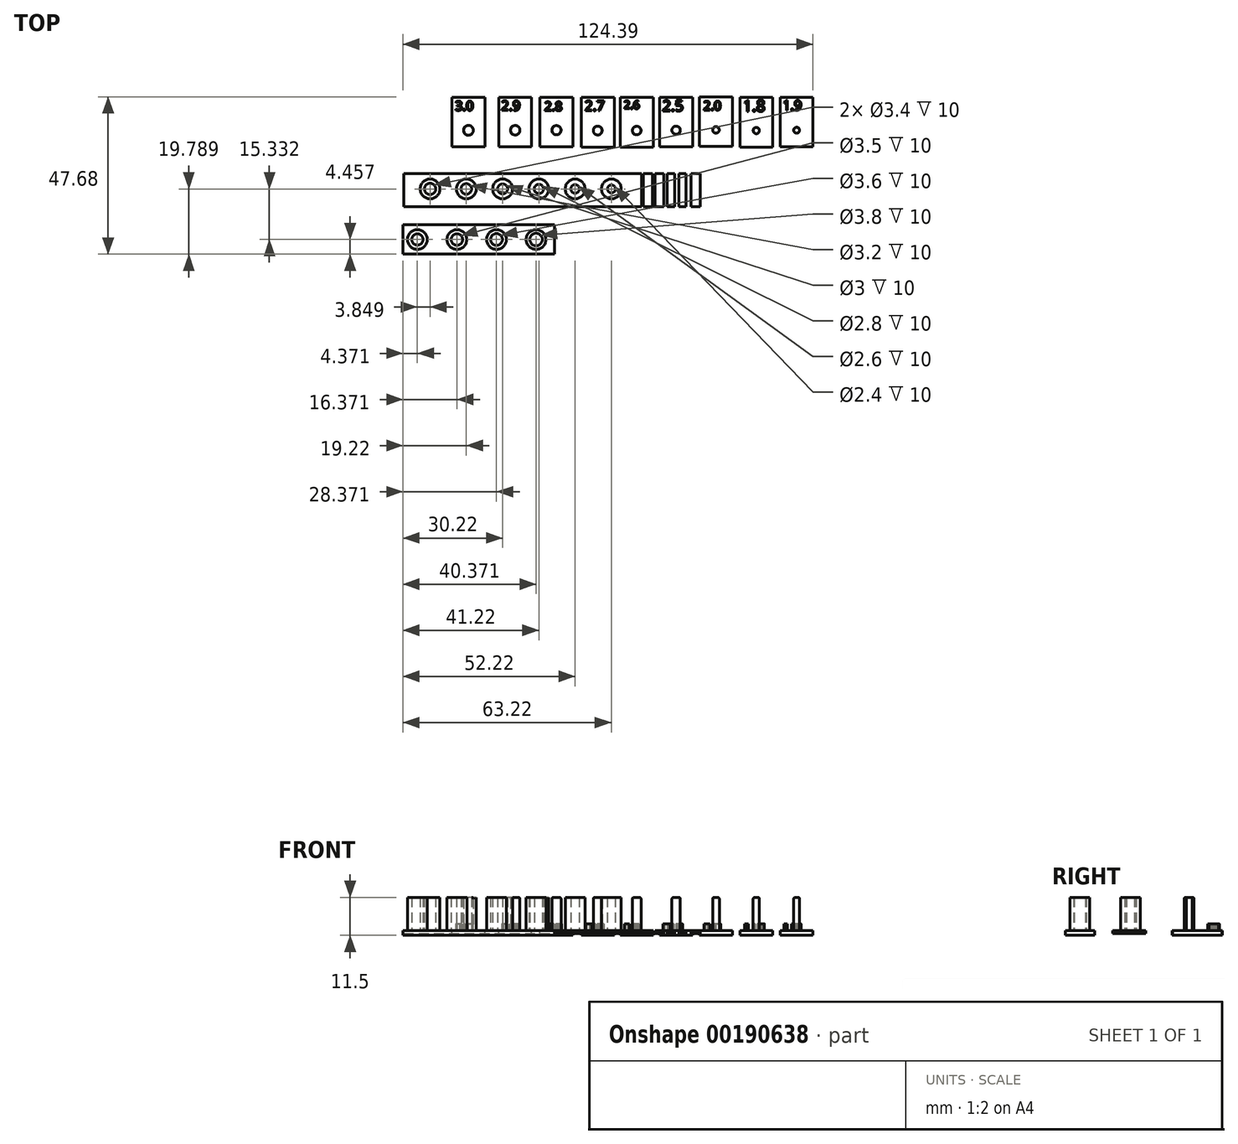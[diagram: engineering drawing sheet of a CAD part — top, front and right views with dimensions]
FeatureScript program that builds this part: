
annotation { "Feature Type Name" : "Feature", "Feature Type Description" : "" }
export const myFeature = defineFeature(function(context is Context, id is Id, definition is map)
    precondition{}
    {
        {
            var Q0;
            Q0=qCreatedBy(makeId("Top.planeOp"),FACE);
            var sketch = newSketch(context, id + "F0", { "sketchPlane" : qUnion([Q0])});
            skLineSegment(sketch, "E0.bottom", {"start": v(-35, 10) * mm, "end": v(55, 10) * mm});
            skLineSegment(sketch, "E0.top", {"start": v(-35, 0) * mm, "end": v(55, 0) * mm});
            skLineSegment(sketch, "E0.left", {"start": v(-35, 10) * mm, "end": v(-35, 0) * mm});
            skLineSegment(sketch, "E0.right", {"start": v(55, 10) * mm, "end": v(55, 0) * mm});
            skCircle(sketch, "E1", {"center": v(-27, 5.35) * mm, "radius": 3 * mm});
            skCircle(sketch, "E2", {"center": v(-16, 5.35) * mm, "radius": 3 * mm});
            skCircle(sketch, "E3", {"center": v(-5, 5.35) * mm, "radius": 3 * mm});
            skCircle(sketch, "E4", {"center": v(6, 5.35) * mm, "radius": 3 * mm});
            skCircle(sketch, "E5", {"center": v(17, 5.35) * mm, "radius": 3 * mm});
            skCircle(sketch, "E6", {"center": v(28, 5.35) * mm, "radius": 3 * mm});
            skCircle(sketch, "E7", {"center": v(28, 5.35) * mm, "radius": 1.2 * mm});
            skCircle(sketch, "E8", {"center": v(17, 5.35) * mm, "radius": 1.3 * mm});
            skCircle(sketch, "E9", {"center": v(6, 5.35) * mm, "radius": 1.4 * mm});
            skCircle(sketch, "E10", {"center": v(-5, 5.35) * mm, "radius": 1.5 * mm});
            skCircle(sketch, "E11", {"center": v(-16, 5.35) * mm, "radius": 1.6 * mm});
            skCircle(sketch, "E12", {"center": v(-27, 5.35) * mm, "radius": 1.7 * mm});
            skLineSegment(sketch, "E13.bottom", {"start": v(52.19, 10) * mm, "end": v(50.69, 10) * mm});
            skLineSegment(sketch, "E13.top", {"start": v(52.19, 0) * mm, "end": v(50.69, 0) * mm});
            skLineSegment(sketch, "E13.left", {"start": v(52.19, 10) * mm, "end": v(52.19, 0) * mm});
            skLineSegment(sketch, "E13.right", {"start": v(50.69, 10) * mm, "end": v(50.69, 0) * mm});
            skLineSegment(sketch, "E14.bottom", {"start": v(48.47, 10) * mm, "end": v(47.22, 10) * mm});
            skLineSegment(sketch, "E14.top", {"start": v(48.47, 0) * mm, "end": v(47.22, 0) * mm});
            skLineSegment(sketch, "E14.left", {"start": v(48.47, 10) * mm, "end": v(48.47, 0) * mm});
            skLineSegment(sketch, "E14.right", {"start": v(47.22, 10) * mm, "end": v(47.22, 0) * mm});
            skLineSegment(sketch, "E15.bottom", {"start": v(44.89, 10) * mm, "end": v(43.89, 10) * mm});
            skLineSegment(sketch, "E15.top", {"start": v(44.89, 0) * mm, "end": v(43.89, 0) * mm});
            skLineSegment(sketch, "E15.left", {"start": v(44.89, 10) * mm, "end": v(44.89, 0) * mm});
            skLineSegment(sketch, "E15.right", {"start": v(43.89, 10) * mm, "end": v(43.89, 0) * mm});
            skLineSegment(sketch, "E16.bottom", {"start": v(41.17, 10) * mm, "end": v(40.42, 10) * mm});
            skLineSegment(sketch, "E16.top", {"start": v(41.17, 0) * mm, "end": v(40.42, 0) * mm});
            skLineSegment(sketch, "E16.left", {"start": v(41.17, 10) * mm, "end": v(41.17, 0) * mm});
            skLineSegment(sketch, "E16.right", {"start": v(40.42, 10) * mm, "end": v(40.42, 0) * mm});
            skLineSegment(sketch, "E17.bottom", {"start": v(37.71, 10) * mm, "end": v(37.21, 10) * mm});
            skLineSegment(sketch, "E17.top", {"start": v(37.71, 0) * mm, "end": v(37.21, 0) * mm});
            skLineSegment(sketch, "E17.left", {"start": v(37.71, 10) * mm, "end": v(37.71, 0) * mm});
            skLineSegment(sketch, "E17.right", {"start": v(37.21, 10) * mm, "end": v(37.21, 0) * mm});
            skSolve(sketch);
        }
        {
            var Q0;
            Q0=makeQuery(id+"F0.imprint","IMPRINT",FACE,{"disambiguationData":[TD([[makeQuery(id+"F0.imprint","IMPRINT",EDGE,{"derivedFrom":sQuery(id+"F0.wireOp",EDGE,"E6")}),1.0]])]});
            var Q1;
            {var subQ0=sQuery(id+"F0.wireOp",EDGE,"E0.right");Q1=makeQuery(id+"F0.imprint","IMPRINT",FACE,{"disambiguationData":[TD([[makeQuery(id+"F0.imprint","IMPRINT",EDGE,{"derivedFrom":subQ0}),-1.0]])]});}
            var Q2;
            {var subQ0=sQuery(id+"F0.wireOp",EDGE,"E16.right");Q2=makeQuery(id+"F0.imprint","IMPRINT",FACE,{"disambiguationData":[TD([[makeQuery(id+"F0.imprint","IMPRINT",EDGE,{"derivedFrom":subQ0}),-1.0]])]});}
            var Q3;
            {var subQ0=sQuery(id+"F0.wireOp",EDGE,"E15.right");Q3=makeQuery(id+"F0.imprint","IMPRINT",FACE,{"disambiguationData":[TD([[makeQuery(id+"F0.imprint","IMPRINT",EDGE,{"derivedFrom":subQ0}),-1.0]])]});}
            var Q4;
            {var subQ0=sQuery(id+"F0.wireOp",EDGE,"E14.right");Q4=makeQuery(id+"F0.imprint","IMPRINT",FACE,{"disambiguationData":[TD([[makeQuery(id+"F0.imprint","IMPRINT",EDGE,{"derivedFrom":subQ0}),-1.0]])]});}
            var Q5;
            {var subQ0=sQuery(id+"F0.wireOp",EDGE,"E13.right");Q5=makeQuery(id+"F0.imprint","IMPRINT",FACE,{"disambiguationData":[TD([[makeQuery(id+"F0.imprint","IMPRINT",EDGE,{"derivedFrom":subQ0}),-1.0]])]});}
            var Q6;
            Q6=makeQuery(id+"F0.imprint","IMPRINT",FACE,{"disambiguationData":[TD([[makeQuery(id+"F0.imprint","IMPRINT",EDGE,{"derivedFrom":sQuery(id+"F0.wireOp",EDGE,"E4")}),1.0]])]});
            var Q7;
            Q7=makeQuery(id+"F0.imprint","IMPRINT",FACE,{"disambiguationData":[TD([[makeQuery(id+"F0.imprint","IMPRINT",EDGE,{"derivedFrom":sQuery(id+"F0.wireOp",EDGE,"E5")}),1.0]])]});
            var Q8;
            Q8=makeQuery(id+"F0.imprint","IMPRINT",FACE,{"disambiguationData":[TD([[makeQuery(id+"F0.imprint","IMPRINT",EDGE,{"derivedFrom":sQuery(id+"F0.wireOp",EDGE,"E9")}),1.0]])]});
            var Q9;
            Q9=makeQuery(id+"F0.imprint","IMPRINT",FACE,{"disambiguationData":[TD([[makeQuery(id+"F0.imprint","IMPRINT",EDGE,{"derivedFrom":sQuery(id+"F0.wireOp",EDGE,"E10")}),1.0]])]});
            var Q10;
            Q10=makeQuery(id+"F0.imprint","IMPRINT",FACE,{"disambiguationData":[TD([[makeQuery(id+"F0.imprint","IMPRINT",EDGE,{"derivedFrom":sQuery(id+"F0.wireOp",EDGE,"E7")}),1.0]])]});
            var Q11;
            Q11=makeQuery(id+"F0.imprint","IMPRINT",FACE,{"disambiguationData":[TD([[makeQuery(id+"F0.imprint","IMPRINT",EDGE,{"derivedFrom":sQuery(id+"F0.wireOp",EDGE,"E8")}),1.0]])]});
            var Q12;
            Q12=makeQuery(id+"F0.imprint","IMPRINT",FACE,{"disambiguationData":[TD([[makeQuery(id+"F0.imprint","IMPRINT",EDGE,{"derivedFrom":sQuery(id+"F0.wireOp",EDGE,"E11")}),1.0]])]});
            var Q13;
            Q13=makeQuery(id+"F0.imprint","IMPRINT",FACE,{"disambiguationData":[TD([[makeQuery(id+"F0.imprint","IMPRINT",EDGE,{"derivedFrom":sQuery(id+"F0.wireOp",EDGE,"E12")}),1.0]])]});
            var Q14;
            Q14=makeQuery(id+"F0.imprint","IMPRINT",FACE,{"disambiguationData":[TD([[makeQuery(id+"F0.imprint","IMPRINT",EDGE,{"derivedFrom":sQuery(id+"F0.wireOp",EDGE,"E1")}),1.0]])]});
            var Q15;
            Q15=makeQuery(id+"F0.imprint","IMPRINT",FACE,{"disambiguationData":[TD([[makeQuery(id+"F0.imprint","IMPRINT",EDGE,{"derivedFrom":sQuery(id+"F0.wireOp",EDGE,"E2")}),1.0]])]});
            var Q16;
            Q16=makeQuery(id+"F0.imprint","IMPRINT",FACE,{"disambiguationData":[TD([[makeQuery(id+"F0.imprint","IMPRINT",EDGE,{"derivedFrom":sQuery(id+"F0.wireOp",EDGE,"E3")}),1.0]])]});
            var Q17;
            {var subQ1=sQuery(id+"F0.wireOp",EDGE,"E0.left");Q17=makeQuery(id+"F0.imprint","IMPRINT",FACE,{"disambiguationData":[TD([[makeQuery(id+"F0.imprint","IMPRINT",EDGE,{"derivedFrom":subQ1}),1.0]])]});}
            var Q18;
            Q18=makeQuery(id+"F0.imprint","IMPRINT",FACE,{"disambiguationData":[TD([[makeQuery(id+"F0.imprint","IMPRINT",EDGE,{"derivedFrom":sQuery(id+"F0.wireOp",EDGE,"E15.bottom")}),1.0]])]});
            var Q19;
            Q19=makeQuery(id+"F0.imprint","IMPRINT",FACE,{"disambiguationData":[TD([[makeQuery(id+"F0.imprint","IMPRINT",EDGE,{"derivedFrom":sQuery(id+"F0.wireOp",EDGE,"E16.bottom")}),1.0]])]});
            var Q20;
            Q20=makeQuery(id+"F0.imprint","IMPRINT",FACE,{"disambiguationData":[TD([[makeQuery(id+"F0.imprint","IMPRINT",EDGE,{"derivedFrom":sQuery(id+"F0.wireOp",EDGE,"E13.bottom")}),1.0]])]});
            var Q21;
            Q21=makeQuery(id+"F0.imprint","IMPRINT",FACE,{"disambiguationData":[TD([[makeQuery(id+"F0.imprint","IMPRINT",EDGE,{"derivedFrom":sQuery(id+"F0.wireOp",EDGE,"E14.bottom")}),1.0]])]});
            var Q22;
            Q22=makeQuery(id+"F0.imprint","IMPRINT",FACE,{"disambiguationData":[TD([[makeQuery(id+"F0.imprint","IMPRINT",EDGE,{"derivedFrom":sQuery(id+"F0.wireOp",EDGE,"E17.bottom")}),1.0]])]});
            extrude(context, id + "F1", {"entities" : qUnion([Q0, Q1, Q2, Q3, Q4, Q5, Q6, Q7, Q8, Q9, Q10, Q11, Q12, Q13, Q14, Q15, Q16, Q17, Q18, Q19, Q20, Q21, Q22]), "oppositeDirection" : true, "depth" : 1 * mm});
        }
        {
            var Q0;
            Q0=makeQuery(id+"F0.imprint","IMPRINT",FACE,{"disambiguationData":[TD([[makeQuery(id+"F0.imprint","IMPRINT",EDGE,{"derivedFrom":sQuery(id+"F0.wireOp",EDGE,"E1")}),1.0]])]});
            var Q1;
            Q1=makeQuery(id+"F0.imprint","IMPRINT",FACE,{"disambiguationData":[TD([[makeQuery(id+"F0.imprint","IMPRINT",EDGE,{"derivedFrom":sQuery(id+"F0.wireOp",EDGE,"E2")}),1.0]])]});
            var Q2;
            Q2=makeQuery(id+"F0.imprint","IMPRINT",FACE,{"disambiguationData":[TD([[makeQuery(id+"F0.imprint","IMPRINT",EDGE,{"derivedFrom":sQuery(id+"F0.wireOp",EDGE,"E3")}),1.0]])]});
            var Q3;
            Q3=makeQuery(id+"F0.imprint","IMPRINT",FACE,{"disambiguationData":[TD([[makeQuery(id+"F0.imprint","IMPRINT",EDGE,{"derivedFrom":sQuery(id+"F0.wireOp",EDGE,"E4")}),1.0]])]});
            var Q4;
            Q4=makeQuery(id+"F0.imprint","IMPRINT",FACE,{"disambiguationData":[TD([[makeQuery(id+"F0.imprint","IMPRINT",EDGE,{"derivedFrom":sQuery(id+"F0.wireOp",EDGE,"E5")}),1.0]])]});
            var Q5;
            Q5=makeQuery(id+"F0.imprint","IMPRINT",FACE,{"disambiguationData":[TD([[makeQuery(id+"F0.imprint","IMPRINT",EDGE,{"derivedFrom":sQuery(id+"F0.wireOp",EDGE,"E6")}),1.0]])]});
            var Q6;
            Q6=makeQuery(id+"F0.imprint","IMPRINT",FACE,{"disambiguationData":[TD([[makeQuery(id+"F0.imprint","IMPRINT",EDGE,{"derivedFrom":sQuery(id+"F0.wireOp",EDGE,"PQmnJwLJ-Gn6O-ht3s-PqNv-8H9YZ1rAoUPC.bottom")}),-1.0]])]});
            var Q7;
            Q7=makeQuery(id+"F0.imprint","IMPRINT",FACE,{"disambiguationData":[TD([[makeQuery(id+"F0.imprint","IMPRINT",EDGE,{"derivedFrom":sQuery(id+"F0.wireOp",EDGE,"UL6PvTcp-d3gB-frWF-roNd-aRTeFT7Vgu0b.bottom")}),-1.0]])]});
            var Q8;
            Q8=makeQuery(id+"F0.imprint","IMPRINT",FACE,{"disambiguationData":[TD([[makeQuery(id+"F0.imprint","IMPRINT",EDGE,{"derivedFrom":sQuery(id+"F0.wireOp",EDGE,"dWqF2f6u-Qhn5-39Qu-3Qdw-AeupGA2DbPDi.bottom")}),-1.0]])]});
            var Q9;
            Q9=makeQuery(id+"F0.imprint","IMPRINT",FACE,{"disambiguationData":[TD([[makeQuery(id+"F0.imprint","IMPRINT",EDGE,{"derivedFrom":sQuery(id+"F0.wireOp",EDGE,"3pZbBdGt-NIDK-vHJ1-jkmm-BDyZuHJENsoI.bottom")}),-1.0]])]});
            var Q10;
            Q10=makeQuery(id+"F0.imprint","IMPRINT",FACE,{"disambiguationData":[TD([[makeQuery(id+"F0.imprint","IMPRINT",EDGE,{"derivedFrom":sQuery(id+"F0.wireOp",EDGE,"8ss7ZRCM-gOKD-5URm-W4XT-u9E1LTYDyoXy.bottom")}),-1.0]])]});
            var Q11;
            Q11=makeQuery(id+"F0.imprint","IMPRINT",FACE,{"disambiguationData":[TD([[makeQuery(id+"F0.imprint","IMPRINT",EDGE,{"derivedFrom":sQuery(id+"F0.wireOp",EDGE,"E17.bottom")}),1.0]])]});
            var Q12;
            Q12=makeQuery(id+"F0.imprint","IMPRINT",FACE,{"disambiguationData":[TD([[makeQuery(id+"F0.imprint","IMPRINT",EDGE,{"derivedFrom":sQuery(id+"F0.wireOp",EDGE,"E16.bottom")}),1.0]])]});
            var Q13;
            Q13=makeQuery(id+"F0.imprint","IMPRINT",FACE,{"disambiguationData":[TD([[makeQuery(id+"F0.imprint","IMPRINT",EDGE,{"derivedFrom":sQuery(id+"F0.wireOp",EDGE,"E15.bottom")}),1.0]])]});
            var Q14;
            Q14=makeQuery(id+"F0.imprint","IMPRINT",FACE,{"disambiguationData":[TD([[makeQuery(id+"F0.imprint","IMPRINT",EDGE,{"derivedFrom":sQuery(id+"F0.wireOp",EDGE,"E14.bottom")}),1.0]])]});
            var Q15;
            Q15=makeQuery(id+"F0.imprint","IMPRINT",FACE,{"disambiguationData":[TD([[makeQuery(id+"F0.imprint","IMPRINT",EDGE,{"derivedFrom":sQuery(id+"F0.wireOp",EDGE,"E13.bottom")}),1.0]])]});
            extrude(context, id + "F2", {"entities" : qUnion([Q0, Q1, Q2, Q3, Q4, Q5, Q6, Q7, Q8, Q9, Q10, Q11, Q12, Q13, Q14, Q15]), "operationType" : NewBodyOperationType.ADD, "depth" : 10 * mm});
        }
        {
            var Q0;
            Q0=qCreatedBy(makeId("Top.planeOp"),FACE);
            var sketch = newSketch(context, id + "F3", { "sketchPlane" : qUnion([Q0])});
            skLineSegment(sketch, "E18.bottom", {"start": v(-35.22, -5.53) * mm, "end": v(10.7, -5.53) * mm});
            skLineSegment(sketch, "E18.top", {"start": v(-35.22, -14.44) * mm, "end": v(10.7, -14.44) * mm});
            skLineSegment(sketch, "E18.left", {"start": v(-35.22, -5.53) * mm, "end": v(-35.22, -14.44) * mm});
            skLineSegment(sketch, "E18.right", {"start": v(10.7, -5.53) * mm, "end": v(10.7, -14.44) * mm});
            skCircle(sketch, "E19", {"center": v(-30.85, -9.98) * mm, "radius": 3 * mm});
            skCircle(sketch, "E20.1.0.0", {"center": v(-18.85, -9.98) * mm, "radius": 3 * mm});
            skCircle(sketch, "E20.2.0.0", {"center": v(-6.85, -9.98) * mm, "radius": 3 * mm});
            skCircle(sketch, "E20.3.0.0", {"center": v(5.15, -9.98) * mm, "radius": 3 * mm});
            skLineSegment(sketch, "E20.direction1", {"start": v(-30.85, -9.98) * mm, "end": v(-18.85, -9.98) * mm, "construction": true});
            skLineSegment(sketch, "E21", {"start": v(10.7, -9.98) * mm, "end": v(-35.22, -9.98) * mm, "construction": true});
            skCircle(sketch, "E22", {"center": v(-30.85, -9.98) * mm, "radius": 1.7 * mm});
            skCircle(sketch, "E23", {"center": v(-18.85, -9.98) * mm, "radius": 1.75 * mm});
            skCircle(sketch, "E24", {"center": v(-6.85, -9.98) * mm, "radius": 1.8 * mm});
            skCircle(sketch, "E25", {"center": v(5.15, -9.98) * mm, "radius": 1.9 * mm});
            skSolve(sketch);
        }
        {
            var Q0;
            Q0=makeQuery(id+"F3.imprint","IMPRINT",FACE,{"disambiguationData":[TD([[makeQuery(id+"F3.imprint","IMPRINT",EDGE,{"derivedFrom":sQuery(id+"F3.wireOp",EDGE,"E22")}),1.0]])]});
            var Q1;
            Q1=makeQuery(id+"F3.imprint","IMPRINT",FACE,{"disambiguationData":[TD([[makeQuery(id+"F3.imprint","IMPRINT",EDGE,{"derivedFrom":sQuery(id+"F3.wireOp",EDGE,"E23")}),1.0]])]});
            var Q2;
            Q2=makeQuery(id+"F3.imprint","IMPRINT",FACE,{"disambiguationData":[TD([[makeQuery(id+"F3.imprint","IMPRINT",EDGE,{"derivedFrom":sQuery(id+"F3.wireOp",EDGE,"E24")}),1.0]])]});
            var Q3;
            Q3=makeQuery(id+"F3.imprint","IMPRINT",FACE,{"disambiguationData":[TD([[makeQuery(id+"F3.imprint","IMPRINT",EDGE,{"derivedFrom":sQuery(id+"F3.wireOp",EDGE,"E25")}),1.0]])]});
            var Q4;
            Q4=makeQuery(id+"F3.imprint","IMPRINT",FACE,{"disambiguationData":[TD([[makeQuery(id+"F3.imprint","IMPRINT",EDGE,{"derivedFrom":sQuery(id+"F3.wireOp",EDGE,"E19")}),1.0]])]});
            var Q5;
            Q5=makeQuery(id+"F3.imprint","IMPRINT",FACE,{"disambiguationData":[TD([[makeQuery(id+"F3.imprint","IMPRINT",EDGE,{"derivedFrom":sQuery(id+"F3.wireOp",EDGE,"E20.1.0.0")}),1.0]])]});
            var Q6;
            Q6=makeQuery(id+"F3.imprint","IMPRINT",FACE,{"disambiguationData":[TD([[makeQuery(id+"F3.imprint","IMPRINT",EDGE,{"derivedFrom":sQuery(id+"F3.wireOp",EDGE,"E18.bottom")}),-1.0]])]});
            var Q7;
            Q7=makeQuery(id+"F3.imprint","IMPRINT",FACE,{"disambiguationData":[TD([[makeQuery(id+"F3.imprint","IMPRINT",EDGE,{"derivedFrom":sQuery(id+"F3.wireOp",EDGE,"E20.2.0.0")}),1.0]])]});
            var Q8;
            Q8=makeQuery(id+"F3.imprint","IMPRINT",FACE,{"disambiguationData":[TD([[makeQuery(id+"F3.imprint","IMPRINT",EDGE,{"derivedFrom":sQuery(id+"F3.wireOp",EDGE,"E20.3.0.0")}),1.0]])]});
            extrude(context, id + "F4", {"entities" : qUnion([Q0, Q1, Q2, Q3, Q4, Q5, Q6, Q7, Q8]), "oppositeDirection" : true, "depth" : 1.5 * mm});
        }
        {
            var Q0;
            Q0=makeQuery(id+"F3.imprint","IMPRINT",FACE,{"disambiguationData":[TD([[makeQuery(id+"F3.imprint","IMPRINT",EDGE,{"derivedFrom":sQuery(id+"F3.wireOp",EDGE,"E19")}),1.0]])]});
            var Q1;
            Q1=makeQuery(id+"F3.imprint","IMPRINT",FACE,{"disambiguationData":[TD([[makeQuery(id+"F3.imprint","IMPRINT",EDGE,{"derivedFrom":sQuery(id+"F3.wireOp",EDGE,"E20.1.0.0")}),1.0]])]});
            var Q2;
            Q2=makeQuery(id+"F3.imprint","IMPRINT",FACE,{"disambiguationData":[TD([[makeQuery(id+"F3.imprint","IMPRINT",EDGE,{"derivedFrom":sQuery(id+"F3.wireOp",EDGE,"E20.2.0.0")}),1.0]])]});
            var Q3;
            Q3=makeQuery(id+"F3.imprint","IMPRINT",FACE,{"disambiguationData":[TD([[makeQuery(id+"F3.imprint","IMPRINT",EDGE,{"derivedFrom":sQuery(id+"F3.wireOp",EDGE,"E20.3.0.0")}),1.0]])]});
            extrude(context, id + "F5", {"entities" : qUnion([Q0, Q1, Q2, Q3]), "operationType" : NewBodyOperationType.ADD, "depth" : 10 * mm});
        }
        {
            var Q0;
            Q0=qCreatedBy(makeId("Top.planeOp"),FACE);
            var sketch = newSketch(context, id + "F6", { "sketchPlane" : qUnion([Q0])});
            skLineSegment(sketch, "E26.bottom", {"start": v(-20.37, 33.1) * mm, "end": v(-10.37, 33.1) * mm});
            skLineSegment(sketch, "E26.top", {"start": v(-20.37, 18.1) * mm, "end": v(-10.37, 18.1) * mm});
            skLineSegment(sketch, "E26.left", {"start": v(-20.37, 33.1) * mm, "end": v(-20.37, 18.1) * mm});
            skLineSegment(sketch, "E26.right", {"start": v(-10.37, 33.1) * mm, "end": v(-10.37, 18.1) * mm});
            skLineSegment(sketch, "E27", {"start": v(-20.37, 28.1) * mm, "end": v(-10.37, 28.1) * mm, "construction": true});
            skLineSegment(sketch, "E28", {"start": v(-10.37, 28.1) * mm, "end": v(-20.37, 18.1) * mm, "construction": true});
            skCircle(sketch, "E29", {"center": v(-15.37, 23.1) * mm, "radius": 1.5 * mm});
            skLineSegment(sketch, "E30.bottom", {"start": v(-6.18, 33.15) * mm, "end": v(3.82, 33.15) * mm});
            skLineSegment(sketch, "E30.top", {"start": v(-6.18, 18.15) * mm, "end": v(3.82, 18.15) * mm});
            skLineSegment(sketch, "E30.left", {"start": v(-6.18, 33.15) * mm, "end": v(-6.18, 18.15) * mm});
            skLineSegment(sketch, "E30.right", {"start": v(3.82, 33.15) * mm, "end": v(3.82, 18.15) * mm});
            skLineSegment(sketch, "E31", {"start": v(-6.18, 28.15) * mm, "end": v(3.82, 28.15) * mm, "construction": true});
            skLineSegment(sketch, "E32", {"start": v(3.82, 28.15) * mm, "end": v(-6.18, 18.15) * mm, "construction": true});
            skCircle(sketch, "E33", {"center": v(-1.18, 23.15) * mm, "radius": 1.45 * mm});
            skLineSegment(sketch, "E34.bottom", {"start": v(6.34, 33.15) * mm, "end": v(16.34, 33.15) * mm});
            skLineSegment(sketch, "E34.top", {"start": v(6.34, 18.15) * mm, "end": v(16.34, 18.15) * mm});
            skLineSegment(sketch, "E34.left", {"start": v(6.34, 33.15) * mm, "end": v(6.34, 18.15) * mm});
            skLineSegment(sketch, "E34.right", {"start": v(16.34, 33.15) * mm, "end": v(16.34, 18.15) * mm});
            skLineSegment(sketch, "E35", {"start": v(6.34, 28.15) * mm, "end": v(16.34, 28.15) * mm, "construction": true});
            skLineSegment(sketch, "E36", {"start": v(16.34, 28.15) * mm, "end": v(6.34, 18.15) * mm, "construction": true});
            skCircle(sketch, "E37", {"center": v(11.34, 23.15) * mm, "radius": 1.4 * mm});
            skLineSegment(sketch, "E38.bottom", {"start": v(18.85, 33.05) * mm, "end": v(28.85, 33.05) * mm});
            skLineSegment(sketch, "E38.top", {"start": v(18.85, 18.05) * mm, "end": v(28.85, 18.05) * mm});
            skLineSegment(sketch, "E38.left", {"start": v(18.85, 33.05) * mm, "end": v(18.85, 18.05) * mm});
            skLineSegment(sketch, "E38.right", {"start": v(28.85, 33.05) * mm, "end": v(28.85, 18.05) * mm});
            skLineSegment(sketch, "E39", {"start": v(18.85, 28.05) * mm, "end": v(28.85, 28.05) * mm, "construction": true});
            skLineSegment(sketch, "E40", {"start": v(28.85, 28.05) * mm, "end": v(18.85, 18.05) * mm, "construction": true});
            skCircle(sketch, "E41", {"center": v(23.85, 23.05) * mm, "radius": 1.35 * mm});
            skLineSegment(sketch, "E42.bottom", {"start": v(30.68, 33.05) * mm, "end": v(40.68, 33.05) * mm});
            skLineSegment(sketch, "E42.top", {"start": v(30.68, 18.05) * mm, "end": v(40.68, 18.05) * mm});
            skLineSegment(sketch, "E42.left", {"start": v(30.68, 33.05) * mm, "end": v(30.68, 18.05) * mm});
            skLineSegment(sketch, "E42.right", {"start": v(40.68, 33.05) * mm, "end": v(40.68, 18.05) * mm});
            skLineSegment(sketch, "E43", {"start": v(30.68, 28.05) * mm, "end": v(40.68, 28.05) * mm, "construction": true});
            skLineSegment(sketch, "E44", {"start": v(40.68, 28.05) * mm, "end": v(30.68, 18.05) * mm, "construction": true});
            skCircle(sketch, "E45", {"center": v(35.68, 23.05) * mm, "radius": 1.3 * mm});
            skLineSegment(sketch, "E46.bottom", {"start": v(42.6, 33.15) * mm, "end": v(52.6, 33.15) * mm});
            skLineSegment(sketch, "E46.top", {"start": v(42.6, 18.15) * mm, "end": v(52.6, 18.15) * mm});
            skLineSegment(sketch, "E46.left", {"start": v(42.6, 33.15) * mm, "end": v(42.6, 18.15) * mm});
            skLineSegment(sketch, "E46.right", {"start": v(52.6, 33.15) * mm, "end": v(52.6, 18.15) * mm});
            skLineSegment(sketch, "E47", {"start": v(42.6, 28.15) * mm, "end": v(52.6, 28.15) * mm, "construction": true});
            skLineSegment(sketch, "E48", {"start": v(52.6, 28.15) * mm, "end": v(42.6, 18.15) * mm, "construction": true});
            skCircle(sketch, "E49", {"center": v(47.6, 23.15) * mm, "radius": 1.25 * mm});
            skText(sketch, "E50", { "text": "3.0", "fontName": "OpenSans-Regular.ttf"});
            skText(sketch, "E51", { "text": "2.9", "fontName": "OpenSans-Regular.ttf"});
            skText(sketch, "E52", { "text": "2.8", "fontName": "OpenSans-Regular.ttf"});
            skText(sketch, "E53", { "text": "2.7", "fontName": "OpenSans-Regular.ttf"});
            skText(sketch, "E54", { "text": "2.6", "fontName": "OpenSans-Regular.ttf"});
            skText(sketch, "E55", { "text": "2.5", "fontName": "OpenSans-Regular.ttf"});
            skLineSegment(sketch, "E56.bottom", {"start": v(54.73, 33.24) * mm, "end": v(64.73, 33.24) * mm});
            skLineSegment(sketch, "E56.top", {"start": v(54.73, 18.24) * mm, "end": v(64.73, 18.24) * mm});
            skLineSegment(sketch, "E56.left", {"start": v(54.73, 33.24) * mm, "end": v(54.73, 18.24) * mm});
            skLineSegment(sketch, "E56.right", {"start": v(64.73, 33.24) * mm, "end": v(64.73, 18.24) * mm});
            skLineSegment(sketch, "E57", {"start": v(54.73, 28.24) * mm, "end": v(64.73, 28.24) * mm, "construction": true});
            skLineSegment(sketch, "E58", {"start": v(64.73, 28.24) * mm, "end": v(54.73, 18.24) * mm, "construction": true});
            skCircle(sketch, "E59", {"center": v(59.73, 23.24) * mm, "radius": 1 * mm});
            skLineSegment(sketch, "E60.bottom", {"start": v(66.95, 33.05) * mm, "end": v(76.95, 33.05) * mm});
            skLineSegment(sketch, "E60.top", {"start": v(66.95, 18.05) * mm, "end": v(76.95, 18.05) * mm});
            skLineSegment(sketch, "E60.left", {"start": v(66.95, 33.05) * mm, "end": v(66.95, 18.05) * mm});
            skLineSegment(sketch, "E60.right", {"start": v(76.95, 33.05) * mm, "end": v(76.95, 18.05) * mm});
            skLineSegment(sketch, "E61", {"start": v(66.95, 28.05) * mm, "end": v(76.95, 28.05) * mm, "construction": true});
            skLineSegment(sketch, "E62", {"start": v(76.95, 28.05) * mm, "end": v(66.95, 18.05) * mm, "construction": true});
            skCircle(sketch, "E63", {"center": v(71.95, 23.05) * mm, "radius": 0.95 * mm});
            skLineSegment(sketch, "E64.bottom", {"start": v(79.17, 33.15) * mm, "end": v(89.17, 33.15) * mm});
            skLineSegment(sketch, "E64.top", {"start": v(79.17, 18.15) * mm, "end": v(89.17, 18.15) * mm});
            skLineSegment(sketch, "E64.left", {"start": v(79.17, 33.15) * mm, "end": v(79.17, 18.15) * mm});
            skLineSegment(sketch, "E64.right", {"start": v(89.17, 33.15) * mm, "end": v(89.17, 18.15) * mm});
            skLineSegment(sketch, "E65", {"start": v(79.17, 28.15) * mm, "end": v(89.17, 28.15) * mm, "construction": true});
            skLineSegment(sketch, "E66", {"start": v(89.17, 28.15) * mm, "end": v(79.17, 18.15) * mm, "construction": true});
            skCircle(sketch, "E67", {"center": v(84.17, 23.15) * mm, "radius": 0.9 * mm});
            skText(sketch, "E68", { "text": "2.0\n", "fontName": "OpenSans-Regular.ttf"});
            skText(sketch, "E69", { "text": "1.8", "fontName": "OpenSans-Regular.ttf"});
            skText(sketch, "E70", { "text": "1.9", "fontName": "OpenSans-Regular.ttf"});
            const initialGuessF6  = {"E50": [-0.01942, 0.02913, 1, 0, 0.00286], "E51": [-0.00542, 0.02913, 1, 0, 0.00296], "E52": [0.00769, 0.02903, 1, 0, 0.00276], "E53": [0.01991, 0.02903, 1, 0, 0.00306], "E54": [0.03174, 0.02963, 1, 0, 0.00246], "E55": [0.04347, 0.02894, 1, 0, 0.00325], "E68": [0.05589, 0.02923, 1, 0, 0.00276], "E69": [0.06791, 0.02884, 1, 0, 0.00345], "E70": [0.07994, 0.02923, 1, 0, 0.00296]};
            skSetInitialGuess(sketch, initialGuessF6);
            skSolve(sketch);
        }
        {
            var Q0;
            Q0 = qSketchRegion(id + "F6", true);
            var Q1;
            Q1=makeQuery(id+"F6.imprint","IMPRINT",FACE,{"disambiguationData":[TD([[makeQuery(id+"F6.imprint","IMPRINT",EDGE,{"derivedFrom":sQuery(id+"F6.wireOp",EDGE,"E68.sketch_text.stroke-36")}),1.0]])]});
            var Q2;
            Q2=makeQuery(id+"F6.imprint","IMPRINT",FACE,{"disambiguationData":[TD([[makeQuery(id+"F6.imprint","IMPRINT",EDGE,{"derivedFrom":sQuery(id+"F6.wireOp",EDGE,"E30.bottom")}),-1.0]])]});
            var Q3;
            Q3=makeQuery(id+"F6.imprint","IMPRINT",FACE,{"disambiguationData":[TD([[makeQuery(id+"F6.imprint","IMPRINT",EDGE,{"derivedFrom":sQuery(id+"F6.wireOp",EDGE,"E34.bottom")}),-1.0]])]});
            var Q4;
            Q4=makeQuery(id+"F6.imprint","IMPRINT",FACE,{"disambiguationData":[TD([[makeQuery(id+"F6.imprint","IMPRINT",EDGE,{"derivedFrom":sQuery(id+"F6.wireOp",EDGE,"E26.bottom")}),-1.0]])]});
            var Q5;
            Q5=makeQuery(id+"F6.imprint","IMPRINT",FACE,{"disambiguationData":[TD([[makeQuery(id+"F6.imprint","IMPRINT",EDGE,{"derivedFrom":sQuery(id+"F6.wireOp",EDGE,"E38.bottom")}),-1.0]])]});
            var Q6;
            Q6=makeQuery(id+"F6.imprint","IMPRINT",FACE,{"disambiguationData":[TD([[makeQuery(id+"F6.imprint","IMPRINT",EDGE,{"derivedFrom":sQuery(id+"F6.wireOp",EDGE,"E42.bottom")}),-1.0]])]});
            var Q7;
            Q7=makeQuery(id+"F6.imprint","IMPRINT",FACE,{"disambiguationData":[TD([[makeQuery(id+"F6.imprint","IMPRINT",EDGE,{"derivedFrom":sQuery(id+"F6.wireOp",EDGE,"E69.sketch_text.stroke-32")}),1.0]])]});
            var Q8;
            Q8=makeQuery(id+"F6.imprint","IMPRINT",FACE,{"disambiguationData":[TD([[makeQuery(id+"F6.imprint","IMPRINT",EDGE,{"derivedFrom":sQuery(id+"F6.wireOp",EDGE,"E46.bottom")}),-1.0]])]});
            var Q9;
            Q9=makeQuery(id+"F6.imprint","IMPRINT",FACE,{"disambiguationData":[TD([[makeQuery(id+"F6.imprint","IMPRINT",EDGE,{"derivedFrom":sQuery(id+"F6.wireOp",EDGE,"E69.sketch_text.stroke-40")}),1.0]])]});
            var Q10;
            Q10=makeQuery(id+"F6.imprint","IMPRINT",FACE,{"disambiguationData":[TD([[makeQuery(id+"F6.imprint","IMPRINT",EDGE,{"derivedFrom":sQuery(id+"F6.wireOp",EDGE,"E56.bottom")}),-1.0]])]});
            var Q11;
            Q11=makeQuery(id+"F6.imprint","IMPRINT",FACE,{"disambiguationData":[TD([[makeQuery(id+"F6.imprint","IMPRINT",EDGE,{"derivedFrom":sQuery(id+"F6.wireOp",EDGE,"E60.bottom")}),-1.0]])]});
            var Q12;
            Q12=makeQuery(id+"F6.imprint","IMPRINT",FACE,{"disambiguationData":[TD([[makeQuery(id+"F6.imprint","IMPRINT",EDGE,{"derivedFrom":sQuery(id+"F6.wireOp",EDGE,"E54.sketch_text.stroke-43")}),1.0]])]});
            var Q13;
            Q13=makeQuery(id+"F6.imprint","IMPRINT",FACE,{"disambiguationData":[TD([[makeQuery(id+"F6.imprint","IMPRINT",EDGE,{"derivedFrom":sQuery(id+"F6.wireOp",EDGE,"E64.bottom")}),-1.0]])]});
            var Q14;
            Q14=makeQuery(id+"F6.imprint","IMPRINT",FACE,{"disambiguationData":[TD([[makeQuery(id+"F6.imprint","IMPRINT",EDGE,{"derivedFrom":sQuery(id+"F6.wireOp",EDGE,"E70.sketch_text.stroke-33")}),1.0]])]});
            var Q15;
            Q15=makeQuery(id+"F6.imprint","IMPRINT",FACE,{"disambiguationData":[TD([[makeQuery(id+"F6.imprint","IMPRINT",EDGE,{"derivedFrom":sQuery(id+"F6.wireOp",EDGE,"E52.sketch_text.stroke-51")}),1.0]])]});
            var Q16;
            Q16=makeQuery(id+"F6.imprint","IMPRINT",FACE,{"disambiguationData":[TD([[makeQuery(id+"F6.imprint","IMPRINT",EDGE,{"derivedFrom":sQuery(id+"F6.wireOp",EDGE,"E52.sketch_text.stroke-43")}),1.0]])]});
            var Q17;
            Q17=makeQuery(id+"F6.imprint","IMPRINT",FACE,{"disambiguationData":[TD([[makeQuery(id+"F6.imprint","IMPRINT",EDGE,{"derivedFrom":sQuery(id+"F6.wireOp",EDGE,"E29")}),1.0]])]});
            var Q18;
            Q18=makeQuery(id+"F6.imprint","IMPRINT",FACE,{"disambiguationData":[TD([[makeQuery(id+"F6.imprint","IMPRINT",EDGE,{"derivedFrom":sQuery(id+"F6.wireOp",EDGE,"E33")}),1.0]])]});
            var Q19;
            Q19=makeQuery(id+"F6.imprint","IMPRINT",FACE,{"disambiguationData":[TD([[makeQuery(id+"F6.imprint","IMPRINT",EDGE,{"derivedFrom":sQuery(id+"F6.wireOp",EDGE,"E37")}),1.0]])]});
            var Q20;
            Q20=makeQuery(id+"F6.imprint","IMPRINT",FACE,{"disambiguationData":[TD([[makeQuery(id+"F6.imprint","IMPRINT",EDGE,{"derivedFrom":sQuery(id+"F6.wireOp",EDGE,"E41")}),1.0]])]});
            var Q21;
            Q21=makeQuery(id+"F6.imprint","IMPRINT",FACE,{"disambiguationData":[TD([[makeQuery(id+"F6.imprint","IMPRINT",EDGE,{"derivedFrom":sQuery(id+"F6.wireOp",EDGE,"E45")}),1.0]])]});
            var Q22;
            Q22=makeQuery(id+"F6.imprint","IMPRINT",FACE,{"disambiguationData":[TD([[makeQuery(id+"F6.imprint","IMPRINT",EDGE,{"derivedFrom":sQuery(id+"F6.wireOp",EDGE,"E49")}),1.0]])]});
            var Q23;
            Q23=makeQuery(id+"F6.imprint","IMPRINT",FACE,{"disambiguationData":[TD([[makeQuery(id+"F6.imprint","IMPRINT",EDGE,{"derivedFrom":sQuery(id+"F6.wireOp",EDGE,"E50.sketch_text.stroke-44")}),1.0]])]});
            var Q24;
            Q24=makeQuery(id+"F6.imprint","IMPRINT",FACE,{"disambiguationData":[TD([[makeQuery(id+"F6.imprint","IMPRINT",EDGE,{"derivedFrom":sQuery(id+"F6.wireOp",EDGE,"E51.sketch_text.stroke-44")}),1.0]])]});
            var Q25;
            Q25=makeQuery(id+"F6.imprint","IMPRINT",FACE,{"disambiguationData":[TD([[makeQuery(id+"F6.imprint","IMPRINT",EDGE,{"derivedFrom":sQuery(id+"F6.wireOp",EDGE,"E69.sketch_text.stroke-0")}),-1.0]])]});
            var Q26;
            Q26=makeQuery(id+"F6.imprint","IMPRINT",FACE,{"disambiguationData":[TD([[makeQuery(id+"F6.imprint","IMPRINT",EDGE,{"derivedFrom":sQuery(id+"F6.wireOp",EDGE,"E68.sketch_text.stroke-20")}),-1.0]])]});
            var Q27;
            Q27=makeQuery(id+"F6.imprint","IMPRINT",FACE,{"disambiguationData":[TD([[makeQuery(id+"F6.imprint","IMPRINT",EDGE,{"derivedFrom":sQuery(id+"F6.wireOp",EDGE,"E53.sketch_text.stroke-0")}),-1.0]])]});
            var Q28;
            Q28=makeQuery(id+"F6.imprint","IMPRINT",FACE,{"disambiguationData":[TD([[makeQuery(id+"F6.imprint","IMPRINT",EDGE,{"derivedFrom":sQuery(id+"F6.wireOp",EDGE,"E53.sketch_text.stroke-20")}),-1.0]])]});
            var Q29;
            Q29=makeQuery(id+"F6.imprint","IMPRINT",FACE,{"disambiguationData":[TD([[makeQuery(id+"F6.imprint","IMPRINT",EDGE,{"derivedFrom":sQuery(id+"F6.wireOp",EDGE,"E53.sketch_text.stroke-28")}),-1.0]])]});
            var Q30;
            Q30=makeQuery(id+"F6.imprint","IMPRINT",FACE,{"disambiguationData":[TD([[makeQuery(id+"F6.imprint","IMPRINT",EDGE,{"derivedFrom":sQuery(id+"F6.wireOp",EDGE,"E54.sketch_text.stroke-0")}),-1.0]])]});
            var Q31;
            Q31=makeQuery(id+"F6.imprint","IMPRINT",FACE,{"disambiguationData":[TD([[makeQuery(id+"F6.imprint","IMPRINT",EDGE,{"derivedFrom":sQuery(id+"F6.wireOp",EDGE,"E70.sketch_text.stroke-0")}),-1.0]])]});
            var Q32;
            Q32=makeQuery(id+"F6.imprint","IMPRINT",FACE,{"disambiguationData":[TD([[makeQuery(id+"F6.imprint","IMPRINT",EDGE,{"derivedFrom":sQuery(id+"F6.wireOp",EDGE,"E54.sketch_text.stroke-20")}),-1.0]])]});
            var Q33;
            Q33=makeQuery(id+"F6.imprint","IMPRINT",FACE,{"disambiguationData":[TD([[makeQuery(id+"F6.imprint","IMPRINT",EDGE,{"derivedFrom":sQuery(id+"F6.wireOp",EDGE,"E50.sketch_text.stroke-36")}),-1.0]])]});
            var Q34;
            Q34=makeQuery(id+"F6.imprint","IMPRINT",FACE,{"disambiguationData":[TD([[makeQuery(id+"F6.imprint","IMPRINT",EDGE,{"derivedFrom":sQuery(id+"F6.wireOp",EDGE,"E55.sketch_text.stroke-0")}),-1.0]])]});
            var Q35;
            Q35=makeQuery(id+"F6.imprint","IMPRINT",FACE,{"disambiguationData":[TD([[makeQuery(id+"F6.imprint","IMPRINT",EDGE,{"derivedFrom":sQuery(id+"F6.wireOp",EDGE,"E51.sketch_text.stroke-28")}),-1.0]])]});
            var Q36;
            Q36=makeQuery(id+"F6.imprint","IMPRINT",FACE,{"disambiguationData":[TD([[makeQuery(id+"F6.imprint","IMPRINT",EDGE,{"derivedFrom":sQuery(id+"F6.wireOp",EDGE,"E55.sketch_text.stroke-20")}),-1.0]])]});
            var Q37;
            Q37=makeQuery(id+"F6.imprint","IMPRINT",FACE,{"disambiguationData":[TD([[makeQuery(id+"F6.imprint","IMPRINT",EDGE,{"derivedFrom":sQuery(id+"F6.wireOp",EDGE,"E54.sketch_text.stroke-28")}),-1.0]])]});
            var Q38;
            Q38=makeQuery(id+"F6.imprint","IMPRINT",FACE,{"disambiguationData":[TD([[makeQuery(id+"F6.imprint","IMPRINT",EDGE,{"derivedFrom":sQuery(id+"F6.wireOp",EDGE,"E55.sketch_text.stroke-28")}),-1.0]])]});
            var Q39;
            Q39=makeQuery(id+"F6.imprint","IMPRINT",FACE,{"disambiguationData":[TD([[makeQuery(id+"F6.imprint","IMPRINT",EDGE,{"derivedFrom":sQuery(id+"F6.wireOp",EDGE,"E68.sketch_text.stroke-28")}),-1.0]])]});
            var Q40;
            Q40=makeQuery(id+"F6.imprint","IMPRINT",FACE,{"disambiguationData":[TD([[makeQuery(id+"F6.imprint","IMPRINT",EDGE,{"derivedFrom":sQuery(id+"F6.wireOp",EDGE,"E59")}),1.0]])]});
            var Q41;
            Q41=makeQuery(id+"F6.imprint","IMPRINT",FACE,{"disambiguationData":[TD([[makeQuery(id+"F6.imprint","IMPRINT",EDGE,{"derivedFrom":sQuery(id+"F6.wireOp",EDGE,"E70.sketch_text.stroke-17")}),-1.0]])]});
            var Q42;
            Q42=makeQuery(id+"F6.imprint","IMPRINT",FACE,{"disambiguationData":[TD([[makeQuery(id+"F6.imprint","IMPRINT",EDGE,{"derivedFrom":sQuery(id+"F6.wireOp",EDGE,"E63")}),1.0]])]});
            var Q43;
            Q43=makeQuery(id+"F6.imprint","IMPRINT",FACE,{"disambiguationData":[TD([[makeQuery(id+"F6.imprint","IMPRINT",EDGE,{"derivedFrom":sQuery(id+"F6.wireOp",EDGE,"E52.sketch_text.stroke-28")}),-1.0]])]});
            var Q44;
            Q44=makeQuery(id+"F6.imprint","IMPRINT",FACE,{"disambiguationData":[TD([[makeQuery(id+"F6.imprint","IMPRINT",EDGE,{"derivedFrom":sQuery(id+"F6.wireOp",EDGE,"E67")}),1.0]])]});
            var Q45;
            Q45=makeQuery(id+"F6.imprint","IMPRINT",FACE,{"disambiguationData":[TD([[makeQuery(id+"F6.imprint","IMPRINT",EDGE,{"derivedFrom":sQuery(id+"F6.wireOp",EDGE,"E69.sketch_text.stroke-17")}),-1.0]])]});
            var Q46;
            Q46=makeQuery(id+"F6.imprint","IMPRINT",FACE,{"disambiguationData":[TD([[makeQuery(id+"F6.imprint","IMPRINT",EDGE,{"derivedFrom":sQuery(id+"F6.wireOp",EDGE,"E68.sketch_text.stroke-0")}),-1.0]])]});
            var Q47;
            Q47=makeQuery(id+"F6.imprint","IMPRINT",FACE,{"disambiguationData":[TD([[makeQuery(id+"F6.imprint","IMPRINT",EDGE,{"derivedFrom":sQuery(id+"F6.wireOp",EDGE,"E52.sketch_text.stroke-20")}),-1.0]])]});
            var Q48;
            Q48=makeQuery(id+"F6.imprint","IMPRINT",FACE,{"disambiguationData":[TD([[makeQuery(id+"F6.imprint","IMPRINT",EDGE,{"derivedFrom":sQuery(id+"F6.wireOp",EDGE,"E50.sketch_text.stroke-0")}),-1.0]])]});
            var Q49;
            Q49=makeQuery(id+"F6.imprint","IMPRINT",FACE,{"disambiguationData":[TD([[makeQuery(id+"F6.imprint","IMPRINT",EDGE,{"derivedFrom":sQuery(id+"F6.wireOp",EDGE,"E50.sketch_text.stroke-28")}),-1.0]])]});
            var Q50;
            Q50=makeQuery(id+"F6.imprint","IMPRINT",FACE,{"disambiguationData":[TD([[makeQuery(id+"F6.imprint","IMPRINT",EDGE,{"derivedFrom":sQuery(id+"F6.wireOp",EDGE,"E51.sketch_text.stroke-0")}),-1.0]])]});
            var Q51;
            Q51=makeQuery(id+"F6.imprint","IMPRINT",FACE,{"disambiguationData":[TD([[makeQuery(id+"F6.imprint","IMPRINT",EDGE,{"derivedFrom":sQuery(id+"F6.wireOp",EDGE,"E52.sketch_text.stroke-0")}),-1.0]])]});
            var Q52;
            Q52=makeQuery(id+"F6.imprint","IMPRINT",FACE,{"disambiguationData":[TD([[makeQuery(id+"F6.imprint","IMPRINT",EDGE,{"derivedFrom":sQuery(id+"F6.wireOp",EDGE,"E69.sketch_text.stroke-9")}),-1.0]])]});
            var Q53;
            Q53=makeQuery(id+"F6.imprint","IMPRINT",FACE,{"disambiguationData":[TD([[makeQuery(id+"F6.imprint","IMPRINT",EDGE,{"derivedFrom":sQuery(id+"F6.wireOp",EDGE,"E70.sketch_text.stroke-9")}),-1.0]])]});
            var Q54;
            Q54=makeQuery(id+"F6.imprint","IMPRINT",FACE,{"disambiguationData":[TD([[makeQuery(id+"F6.imprint","IMPRINT",EDGE,{"derivedFrom":sQuery(id+"F6.wireOp",EDGE,"E51.sketch_text.stroke-20")}),-1.0]])]});
            extrude(context, id + "F7", {"entities" : qUnion([Q0, Q1, Q2, Q3, Q4, Q5, Q6, Q7, Q8, Q9, Q10, Q11, Q12, Q13, Q14, Q15, Q16, Q17, Q18, Q19, Q20, Q21, Q22, Q23, Q24, Q25, Q26, Q27, Q28, Q29, Q30, Q31, Q32, Q33, Q34, Q35, Q36, Q37, Q38, Q39, Q40, Q41, Q42, Q43, Q44, Q45, Q46, Q47, Q48, Q49, Q50, Q51, Q52, Q53, Q54]), "oppositeDirection" : true, "depth" : 1.5 * mm});
        }
        {
            var Q0;
            Q0=makeQuery(id+"F6.imprint","IMPRINT",FACE,{"disambiguationData":[TD([[makeQuery(id+"F6.imprint","IMPRINT",EDGE,{"derivedFrom":sQuery(id+"F6.wireOp",EDGE,"E29")}),1.0]])]});
            var Q1;
            Q1=makeQuery(id+"F6.imprint","IMPRINT",FACE,{"disambiguationData":[TD([[makeQuery(id+"F6.imprint","IMPRINT",EDGE,{"derivedFrom":sQuery(id+"F6.wireOp",EDGE,"E33")}),1.0]])]});
            var Q2;
            Q2=makeQuery(id+"F6.imprint","IMPRINT",FACE,{"disambiguationData":[TD([[makeQuery(id+"F6.imprint","IMPRINT",EDGE,{"derivedFrom":sQuery(id+"F6.wireOp",EDGE,"E37")}),1.0]])]});
            var Q3;
            Q3=makeQuery(id+"F6.imprint","IMPRINT",FACE,{"disambiguationData":[TD([[makeQuery(id+"F6.imprint","IMPRINT",EDGE,{"derivedFrom":sQuery(id+"F6.wireOp",EDGE,"E41")}),1.0]])]});
            var Q4;
            Q4=makeQuery(id+"F6.imprint","IMPRINT",FACE,{"disambiguationData":[TD([[makeQuery(id+"F6.imprint","IMPRINT",EDGE,{"derivedFrom":sQuery(id+"F6.wireOp",EDGE,"E45")}),1.0]])]});
            var Q5;
            Q5=makeQuery(id+"F6.imprint","IMPRINT",FACE,{"disambiguationData":[TD([[makeQuery(id+"F6.imprint","IMPRINT",EDGE,{"derivedFrom":sQuery(id+"F6.wireOp",EDGE,"E49")}),1.0]])]});
            var Q6;
            Q6=makeQuery(id+"F6.imprint","IMPRINT",FACE,{"disambiguationData":[TD([[makeQuery(id+"F6.imprint","IMPRINT",EDGE,{"derivedFrom":sQuery(id+"F6.wireOp",EDGE,"E59")}),1.0]])]});
            var Q7;
            Q7=makeQuery(id+"F6.imprint","IMPRINT",FACE,{"disambiguationData":[TD([[makeQuery(id+"F6.imprint","IMPRINT",EDGE,{"derivedFrom":sQuery(id+"F6.wireOp",EDGE,"E63")}),1.0]])]});
            var Q8;
            Q8=makeQuery(id+"F6.imprint","IMPRINT",FACE,{"disambiguationData":[TD([[makeQuery(id+"F6.imprint","IMPRINT",EDGE,{"derivedFrom":sQuery(id+"F6.wireOp",EDGE,"E67")}),1.0]])]});
            extrude(context, id + "F8", {"entities" : qUnion([Q0, Q1, Q2, Q3, Q4, Q5, Q6, Q7, Q8]), "operationType" : NewBodyOperationType.ADD, "depth" : 10 * mm});
        }
        {
            var Q0;
            Q0=makeQuery(id+"F6.imprint","IMPRINT",FACE,{"disambiguationData":[TD([[makeQuery(id+"F6.imprint","IMPRINT",EDGE,{"derivedFrom":sQuery(id+"F6.wireOp",EDGE,"E50.sketch_text.stroke-0")}),-1.0]])]});
            var Q1;
            Q1=makeQuery(id+"F6.imprint","IMPRINT",FACE,{"disambiguationData":[TD([[makeQuery(id+"F6.imprint","IMPRINT",EDGE,{"derivedFrom":sQuery(id+"F6.wireOp",EDGE,"E50.sketch_text.stroke-36")}),-1.0]])]});
            var Q2;
            Q2=makeQuery(id+"F6.imprint","IMPRINT",FACE,{"disambiguationData":[TD([[makeQuery(id+"F6.imprint","IMPRINT",EDGE,{"derivedFrom":sQuery(id+"F6.wireOp",EDGE,"E50.sketch_text.stroke-28")}),-1.0]])]});
            var Q3;
            Q3=makeQuery(id+"F6.imprint","IMPRINT",FACE,{"disambiguationData":[TD([[makeQuery(id+"F6.imprint","IMPRINT",EDGE,{"derivedFrom":sQuery(id+"F6.wireOp",EDGE,"E51.sketch_text.stroke-0")}),-1.0]])]});
            var Q4;
            Q4=makeQuery(id+"F6.imprint","IMPRINT",FACE,{"disambiguationData":[TD([[makeQuery(id+"F6.imprint","IMPRINT",EDGE,{"derivedFrom":sQuery(id+"F6.wireOp",EDGE,"E51.sketch_text.stroke-28")}),-1.0]])]});
            var Q5;
            Q5=makeQuery(id+"F6.imprint","IMPRINT",FACE,{"disambiguationData":[TD([[makeQuery(id+"F6.imprint","IMPRINT",EDGE,{"derivedFrom":sQuery(id+"F6.wireOp",EDGE,"E51.sketch_text.stroke-20")}),-1.0]])]});
            var Q6;
            Q6=makeQuery(id+"F6.imprint","IMPRINT",FACE,{"disambiguationData":[TD([[makeQuery(id+"F6.imprint","IMPRINT",EDGE,{"derivedFrom":sQuery(id+"F6.wireOp",EDGE,"E52.sketch_text.stroke-0")}),-1.0]])]});
            var Q7;
            Q7=makeQuery(id+"F6.imprint","IMPRINT",FACE,{"disambiguationData":[TD([[makeQuery(id+"F6.imprint","IMPRINT",EDGE,{"derivedFrom":sQuery(id+"F6.wireOp",EDGE,"E52.sketch_text.stroke-20")}),-1.0]])]});
            var Q8;
            Q8=makeQuery(id+"F6.imprint","IMPRINT",FACE,{"disambiguationData":[TD([[makeQuery(id+"F6.imprint","IMPRINT",EDGE,{"derivedFrom":sQuery(id+"F6.wireOp",EDGE,"E52.sketch_text.stroke-28")}),-1.0]])]});
            var Q9;
            Q9=makeQuery(id+"F6.imprint","IMPRINT",FACE,{"disambiguationData":[TD([[makeQuery(id+"F6.imprint","IMPRINT",EDGE,{"derivedFrom":sQuery(id+"F6.wireOp",EDGE,"E53.sketch_text.stroke-0")}),-1.0]])]});
            var Q10;
            Q10=makeQuery(id+"F6.imprint","IMPRINT",FACE,{"disambiguationData":[TD([[makeQuery(id+"F6.imprint","IMPRINT",EDGE,{"derivedFrom":sQuery(id+"F6.wireOp",EDGE,"E53.sketch_text.stroke-20")}),-1.0]])]});
            var Q11;
            Q11=makeQuery(id+"F6.imprint","IMPRINT",FACE,{"disambiguationData":[TD([[makeQuery(id+"F6.imprint","IMPRINT",EDGE,{"derivedFrom":sQuery(id+"F6.wireOp",EDGE,"E53.sketch_text.stroke-28")}),-1.0]])]});
            var Q12;
            Q12=makeQuery(id+"F6.imprint","IMPRINT",FACE,{"disambiguationData":[TD([[makeQuery(id+"F6.imprint","IMPRINT",EDGE,{"derivedFrom":sQuery(id+"F6.wireOp",EDGE,"E54.sketch_text.stroke-0")}),-1.0]])]});
            var Q13;
            Q13=makeQuery(id+"F6.imprint","IMPRINT",FACE,{"disambiguationData":[TD([[makeQuery(id+"F6.imprint","IMPRINT",EDGE,{"derivedFrom":sQuery(id+"F6.wireOp",EDGE,"E54.sketch_text.stroke-20")}),-1.0]])]});
            var Q14;
            Q14=makeQuery(id+"F6.imprint","IMPRINT",FACE,{"disambiguationData":[TD([[makeQuery(id+"F6.imprint","IMPRINT",EDGE,{"derivedFrom":sQuery(id+"F6.wireOp",EDGE,"E54.sketch_text.stroke-28")}),-1.0]])]});
            var Q15;
            Q15=makeQuery(id+"F6.imprint","IMPRINT",FACE,{"disambiguationData":[TD([[makeQuery(id+"F6.imprint","IMPRINT",EDGE,{"derivedFrom":sQuery(id+"F6.wireOp",EDGE,"E55.sketch_text.stroke-0")}),-1.0]])]});
            var Q16;
            Q16=makeQuery(id+"F6.imprint","IMPRINT",FACE,{"disambiguationData":[TD([[makeQuery(id+"F6.imprint","IMPRINT",EDGE,{"derivedFrom":sQuery(id+"F6.wireOp",EDGE,"E55.sketch_text.stroke-20")}),-1.0]])]});
            var Q17;
            Q17=makeQuery(id+"F6.imprint","IMPRINT",FACE,{"disambiguationData":[TD([[makeQuery(id+"F6.imprint","IMPRINT",EDGE,{"derivedFrom":sQuery(id+"F6.wireOp",EDGE,"E55.sketch_text.stroke-28")}),-1.0]])]});
            var Q18;
            Q18=makeQuery(id+"F6.imprint","IMPRINT",FACE,{"disambiguationData":[TD([[makeQuery(id+"F6.imprint","IMPRINT",EDGE,{"derivedFrom":sQuery(id+"F6.wireOp",EDGE,"E68.sketch_text.stroke-0")}),-1.0]])]});
            var Q19;
            Q19=makeQuery(id+"F6.imprint","IMPRINT",FACE,{"disambiguationData":[TD([[makeQuery(id+"F6.imprint","IMPRINT",EDGE,{"derivedFrom":sQuery(id+"F6.wireOp",EDGE,"E68.sketch_text.stroke-20")}),-1.0]])]});
            var Q20;
            Q20=makeQuery(id+"F6.imprint","IMPRINT",FACE,{"disambiguationData":[TD([[makeQuery(id+"F6.imprint","IMPRINT",EDGE,{"derivedFrom":sQuery(id+"F6.wireOp",EDGE,"E68.sketch_text.stroke-28")}),-1.0]])]});
            var Q21;
            Q21=makeQuery(id+"F6.imprint","IMPRINT",FACE,{"disambiguationData":[TD([[makeQuery(id+"F6.imprint","IMPRINT",EDGE,{"derivedFrom":sQuery(id+"F6.wireOp",EDGE,"E69.sketch_text.stroke-0")}),-1.0]])]});
            var Q22;
            Q22=makeQuery(id+"F6.imprint","IMPRINT",FACE,{"disambiguationData":[TD([[makeQuery(id+"F6.imprint","IMPRINT",EDGE,{"derivedFrom":sQuery(id+"F6.wireOp",EDGE,"E69.sketch_text.stroke-9")}),-1.0]])]});
            var Q23;
            Q23=makeQuery(id+"F6.imprint","IMPRINT",FACE,{"disambiguationData":[TD([[makeQuery(id+"F6.imprint","IMPRINT",EDGE,{"derivedFrom":sQuery(id+"F6.wireOp",EDGE,"E69.sketch_text.stroke-17")}),-1.0]])]});
            var Q24;
            Q24=makeQuery(id+"F6.imprint","IMPRINT",FACE,{"disambiguationData":[TD([[makeQuery(id+"F6.imprint","IMPRINT",EDGE,{"derivedFrom":sQuery(id+"F6.wireOp",EDGE,"E70.sketch_text.stroke-0")}),-1.0]])]});
            var Q25;
            Q25=makeQuery(id+"F6.imprint","IMPRINT",FACE,{"disambiguationData":[TD([[makeQuery(id+"F6.imprint","IMPRINT",EDGE,{"derivedFrom":sQuery(id+"F6.wireOp",EDGE,"E70.sketch_text.stroke-17")}),-1.0]])]});
            var Q26;
            Q26=makeQuery(id+"F6.imprint","IMPRINT",FACE,{"disambiguationData":[TD([[makeQuery(id+"F6.imprint","IMPRINT",EDGE,{"derivedFrom":sQuery(id+"F6.wireOp",EDGE,"E70.sketch_text.stroke-9")}),-1.0]])]});
            extrude(context, id + "F9", {"entities" : qUnion([Q0, Q1, Q2, Q3, Q4, Q5, Q6, Q7, Q8, Q9, Q10, Q11, Q12, Q13, Q14, Q15, Q16, Q17, Q18, Q19, Q20, Q21, Q22, Q23, Q24, Q25, Q26]), "operationType" : NewBodyOperationType.ADD, "depth" : 2 * mm});
        }
        {
            var Q0;
            Q0=makeQuery(id+"F8.opExtrude","CAP_EDGE",EDGE,{"disambiguationData":[OSD([sQuery(id+"F6.wireOp",EDGE,"E29")])],"isStart":false});
            var Q1;
            Q1=makeQuery(id+"F8.opExtrude","CAP_EDGE",EDGE,{"disambiguationData":[OSD([sQuery(id+"F6.wireOp",EDGE,"E33")])],"isStart":false});
            var Q2;
            Q2=makeQuery(id+"F8.opExtrude","CAP_EDGE",EDGE,{"disambiguationData":[OSD([sQuery(id+"F6.wireOp",EDGE,"E37")])],"isStart":false});
            var Q3;
            Q3=makeQuery(id+"F8.opExtrude","CAP_EDGE",EDGE,{"disambiguationData":[OSD([sQuery(id+"F6.wireOp",EDGE,"E41")])],"isStart":false});
            var Q4;
            Q4=makeQuery(id+"F8.opExtrude","CAP_EDGE",EDGE,{"disambiguationData":[OSD([sQuery(id+"F6.wireOp",EDGE,"E45")])],"isStart":false});
            var Q5;
            Q5=makeQuery(id+"F8.opExtrude","CAP_EDGE",EDGE,{"disambiguationData":[OSD([sQuery(id+"F6.wireOp",EDGE,"E49")])],"isStart":false});
            var Q6;
            Q6=makeQuery(id+"F8.opExtrude","CAP_EDGE",EDGE,{"disambiguationData":[OSD([sQuery(id+"F6.wireOp",EDGE,"E59")])],"isStart":false});
            var Q7;
            Q7=makeQuery(id+"F8.opExtrude","CAP_EDGE",EDGE,{"disambiguationData":[OSD([sQuery(id+"F6.wireOp",EDGE,"E63")])],"isStart":false});
            var Q8;
            Q8=makeQuery(id+"F8.opExtrude","CAP_EDGE",EDGE,{"disambiguationData":[OSD([sQuery(id+"F6.wireOp",EDGE,"E67")])],"isStart":false});
            fillet(context, id + "F10", {"entities" : qUnion([Q0, Q1, Q2, Q3, Q4, Q5, Q6, Q7, Q8]), "radius" : 0.5 * mm, "tangentPropagation" : true, "rho" : 0.5, "crossSection" : FilletCrossSection.CONIC, "allowEdgeOverflow" : false});
        }
    });
